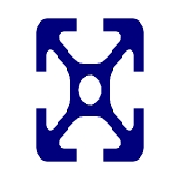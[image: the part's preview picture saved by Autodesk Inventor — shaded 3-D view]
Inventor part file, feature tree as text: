
AUTODESK INVENTOR PART (.ipt)
format: ipt  version: 2020 (Build 240168000, 168)  size: 272,384 bytes
history: native  units: mm
features: other x16, sketch x8, plane x1, split x1
ambient origin geometry x8: Origin, YZ Plane, XZ Plane, XY Plane, X Axis, Y Axis, Z Axis, Center Point
bodies: Body (feature_tree)
feature tree (26):
  other  "Řízená délka"
  other  "Těleso1"
  other  "Start Plane"
  other  "End Plane"
  other  "iFeatureSketch"
  other  "DRAZKA_20:1"
  other  "DRAZKA_20:2"
  other  "DRAZKA_20:3"
  other  "DRAZKA_20:4"
  other  "DIRA_20:1"
  other  "DRAZKA_20:1Axis"
  other  "DRAZKA_20:2Axis"
  other  "DRAZKA_20:3Axis"
  other  "DRAZKA_20:4Axis"
  other  "DIRA_20:1Axis"
  plane  "Work Plane5"
  split  "Split1"
  sketch  "Sketch"  dims[d2=20.0mm d3=20.0mm d4=2.0mm d9=10.0mm d10=100.0mm d11=0.13mm d12=0.0mm d15=0.83mm d16=0.83mm d17=9.8mm d18=3.0mm d19=4.55mm d20=45.0deg d21=5.2mm d22=1.8mm d24=1.0mm d26=0.83mm d27=0.83mm d28=9.8mm d29=3.0mm d30=4.55mm d31=45.0deg d32=5.2mm d33=1.8mm d35=1.0mm d37=0.83mm d38=0.83mm d39=9.8mm d40=3.0mm d41=4.55mm d42=45.0deg d43=5.2mm d44=1.8mm d46=1.0mm d48=0.83mm d49=0.83mm d50=9.8mm d51=3.0mm d52=4.55mm d53=45.0deg d54=5.2mm d55=1.8mm d57=1.0mm d59=4.3mm d60=0.0mm d61=0.0mm d62=0.0mm d63=0.0mm d64=0.0mm d65=0.0mm d66=0.0mm d67=0.0mm d76=90.0deg d14=90.0mm]
  sketch  "Náčrt11"
  other  "Pracovní rovina4"
  sketch  "Náčrt12"
  sketch  "Náčrt6"
  sketch  "Náčrt7"
  sketch  "Náčrt8"
  sketch  "Náčrt9"
  sketch  "Náčrt10"
